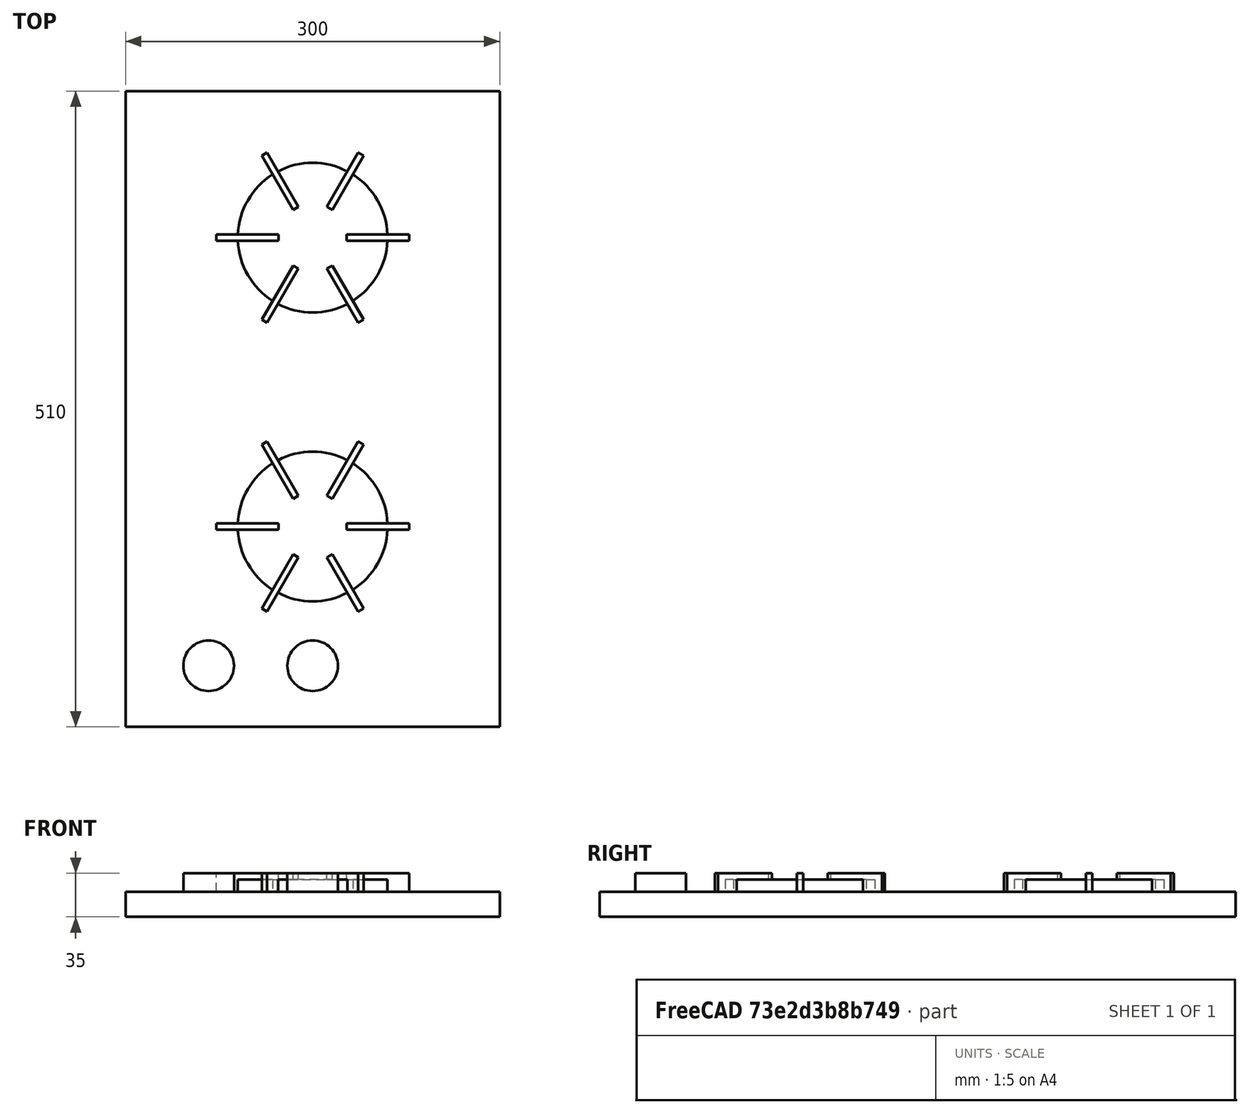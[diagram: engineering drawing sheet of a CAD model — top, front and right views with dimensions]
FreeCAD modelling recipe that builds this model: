
FCSTD DOCUMENT  (FreeCAD 0.21R33668 +26 (Git))
Label: cooktop 2 bocas
License: All rights reserved
objects: Part::Part2DObjectPython×4, Part::Extrusion×4, Part::FeaturePython×3, Part::MultiFuse×1, Part::Compound×1
note: 13 computed .brp shape members not serialized (recipe doc carries the construction recipe); baked Part::Feature solids carry a one-line shape summary decoded from their .brp

FEATURE [Part::Part2DObjectPython] Circle  # Draft 2D object (typed FeaturePython)
  Area = 11309.7
  FirstAngle = 0
  LastAngle = 0
  MakeFace = true
  Radius = 60
FEATURE [Part::Part2DObjectPython] Circle001  # Draft 2D object (typed FeaturePython)
  Area = 1296.59
  FirstAngle = 0
  LastAngle = 0
  MakeFace = true
  Radius = 20.3154
FEATURE [Part::Extrusion] Extrude067  label="Extrude093"
  Base = -> Circle
  Dir = (0,0,1)
  DirMode = 2
  FaceMakerClass = Part::FaceMakerBullseye
  LengthFwd = 10
  LengthRev = 0
  Solid = false
  Symmetric = false
FEATURE [Part::Extrusion] Extrude068  label="Extrude094"
  Base = -> Circle001
  Dir = (0,0,1)
  DirMode = 2
  FaceMakerClass = Part::FaceMakerBullseye
  LengthFwd = 15
  LengthRev = 0
  Placement = pos=(150,-651.018,20) rot=(0,0,1;0rad)
  Solid = false
  Symmetric = false
FEATURE [Part::FeaturePython] Clone082  label="Extrude095"  # Draft clone (typed FeaturePython)
  AttacherType = Attacher::AttachEngine3D
  Fuse = false
  Objects = -> [Extrude068]
  Placement = pos=(66.5733,-651.018,20) rot=(0,0,1;0rad)
  Scale = (1,1,1)
FEATURE [Part::Part2DObjectPython] Rectangle029  # Draft 2D object (typed FeaturePython)
  Area = 153000
  ChamferSize = 0
  Columns = 1
  FilletRadius = 0
  Height = 510
  Length = 300
  MakeFace = true
  Placement = pos=(0,-700,0) rot=(0,0,1;0rad)
  Rows = 1
FEATURE [Part::Extrusion] Extrude065
  Base = -> Rectangle029
  Dir = (0,0,1)
  DirMode = 2
  FaceMakerClass = Part::FaceMakerBullseye
  LengthFwd = 20
  LengthRev = 0
  Solid = false
  Symmetric = false
FEATURE [Part::Part2DObjectPython] Rectangle030  # Draft 2D object (typed FeaturePython)
  Area = 250
  ChamferSize = 0
  Columns = 1
  FilletRadius = 0
  Height = 5
  Length = 50
  MakeFace = true
  Placement = pos=(27.2707,-2.5,0) rot=(0,0,1;0rad)
  Rows = 1
FEATURE [Part::FeaturePython] Array019  # Draft array (typed FeaturePython)
  Angle = 360
  ArrayType = 1
  Axis = (0,0,1)
  Base = -> Rectangle030
  Center = (0,0,0)
  Count = 6
  Fuse = true
  IntervalAxis = (0,0,0)
  IntervalX = (100,0,0)
  IntervalY = (0,100,0)
  IntervalZ = (0,0,100)
  NumberCircles = 3
  NumberPolar = 6
  NumberX = 2
  NumberY = 1
  NumberZ = 1
  RadialDistance = 50
  Symmetry = 1
  TangentialDistance = 25
FEATURE [Part::Extrusion] Extrude066  label="Extrude092"
  Base = -> Array019
  Dir = (0,0,1)
  DirMode = 2
  FaceMakerClass = Part::FaceMakerBullseye
  LengthFwd = 15
  LengthRev = 0
  Solid = false
  Symmetric = false
FEATURE [Part::MultiFuse] Fusion045
  Placement = pos=(150,-307.572,20) rot=(0,0,1;0rad)
  Shapes = -> [Extrude066,Extrude067]
FEATURE [Part::FeaturePython] Clone081  label="Fusion046"  # Draft clone (typed FeaturePython)
  AttacherType = Attacher::AttachEngine3D
  Fuse = false
  Objects = -> [Fusion045]
  Placement = pos=(150,-539.327,20) rot=(0,0,1;0rad)
  Scale = (1,1,1)
FEATURE [Part::Compound] Compound018  label="cooktop"
  Links = -> [Clone081,Extrude068,Clone082,Fusion045,Extrude065]
